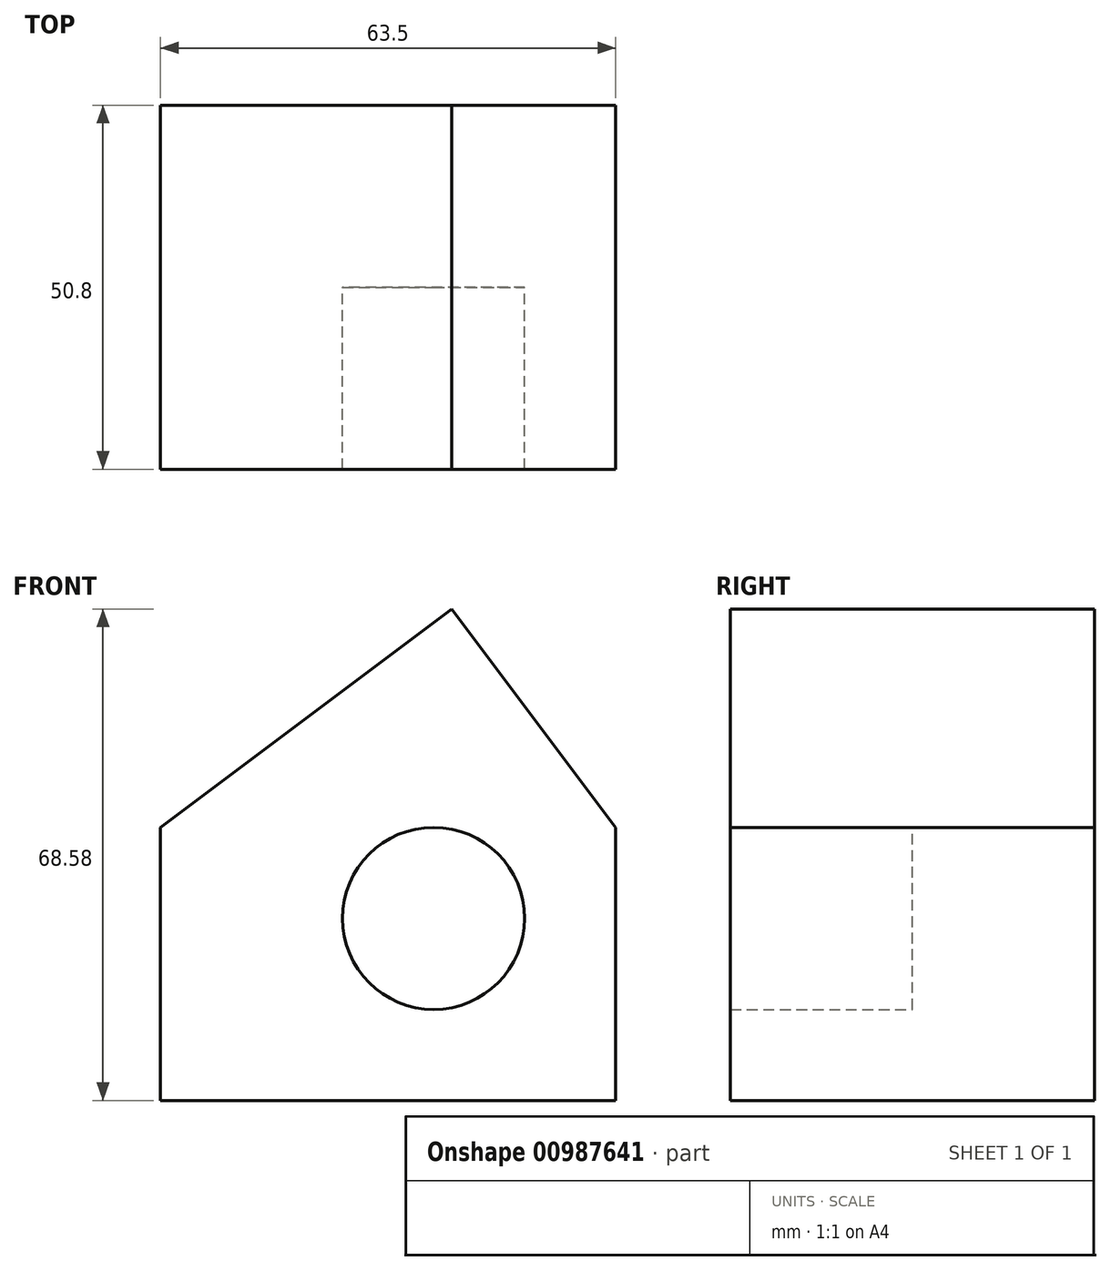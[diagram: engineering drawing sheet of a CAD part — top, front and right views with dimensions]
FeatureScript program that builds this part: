
annotation { "Feature Type Name" : "Feature", "Feature Type Description" : "" }
export const myFeature = defineFeature(function(context is Context, id is Id, definition is map)
    precondition{}
    {
        {
            var Q0;
            Q0=qCreatedBy(makeId("Front.planeOp"),FACE);
            var sketch = newSketch(context, id + "F0", { "sketchPlane" : qUnion([Q0])});
            skLineSegment(sketch, "E0.bottom", {"start": v(0, 0) * mm, "end": v(63.5, 0) * mm});
            skLineSegment(sketch, "E0.top", {"start": v(0, 38.1) * mm, "end": v(63.5, 38.1) * mm});
            skLineSegment(sketch, "E0.left", {"start": v(0, 0) * mm, "end": v(0, 38.1) * mm});
            skLineSegment(sketch, "E0.right", {"start": v(63.5, 0) * mm, "end": v(63.5, 38.1) * mm});
            skLineSegment(sketch, "E1", {"start": v(0, 38.1) * mm, "end": v(40.64, 68.58) * mm});
            skLineSegment(sketch, "E2", {"start": v(40.64, 68.58) * mm, "end": v(63.5, 38.1) * mm});
            skSolve(sketch);
        }
        {
            var Q0;
            Q0=makeQuery(id+"F0.imprint","IMPRINT",FACE,{"disambiguationData":[TD([[makeQuery(id+"F0.imprint","IMPRINT",EDGE,{"derivedFrom":sQuery(id+"F0.wireOp",EDGE,"E0.top")}),1.0]])]});
            var Q1;
            Q1=makeQuery(id+"F0.imprint","IMPRINT",FACE,{"disambiguationData":[TD([[makeQuery(id+"F0.imprint","IMPRINT",EDGE,{"derivedFrom":sQuery(id+"F0.wireOp",EDGE,"E0.bottom")}),1.0]])]});
            extrude(context, id + "F1", {"entities" : qUnion([Q0, Q1]), "depth" : 25.4 * mm, "offsetDistance" : 25.4 * mm});
        }
        {
            var Q0;
            Q0=makeQuery(id+"F1.opExtrude","CAP_FACE",FACE,{"disambiguationData":[OSD([sQuery(id+"F0.wireOp",EDGE,"E0.bottom"),sQuery(id+"F0.wireOp",EDGE,"E0.left"),sQuery(id+"F0.wireOp",EDGE,"E0.right"),sQuery(id+"F0.wireOp",EDGE,"E1"),sQuery(id+"F0.wireOp",EDGE,"E2")])],"isStart":false});
            var sketch = newSketch(context, id + "F2", { "sketchPlane" : qUnion([Q0])});
            skCircle(sketch, "E3", {"center": v(38.1, 25.4) * mm, "radius": 12.7 * mm});
            skSolve(sketch);
        }
        {
            var Q0;
            Q0=makeQuery(id+"F2.imprint","IMPRINT",FACE,{"disambiguationData":[TD([[makeQuery(id+"F2.imprint","IMPRINT",EDGE,{"derivedFrom":sQuery(id+"F2.wireOp",EDGE,"E3")}),-1.0]])]});
            extrude(context, id + "F3", {"entities" : qUnion([Q0]), "operationType" : NewBodyOperationType.ADD, "depth" : 25.4 * mm, "offsetDistance" : 25.4 * mm});
        }
    });
